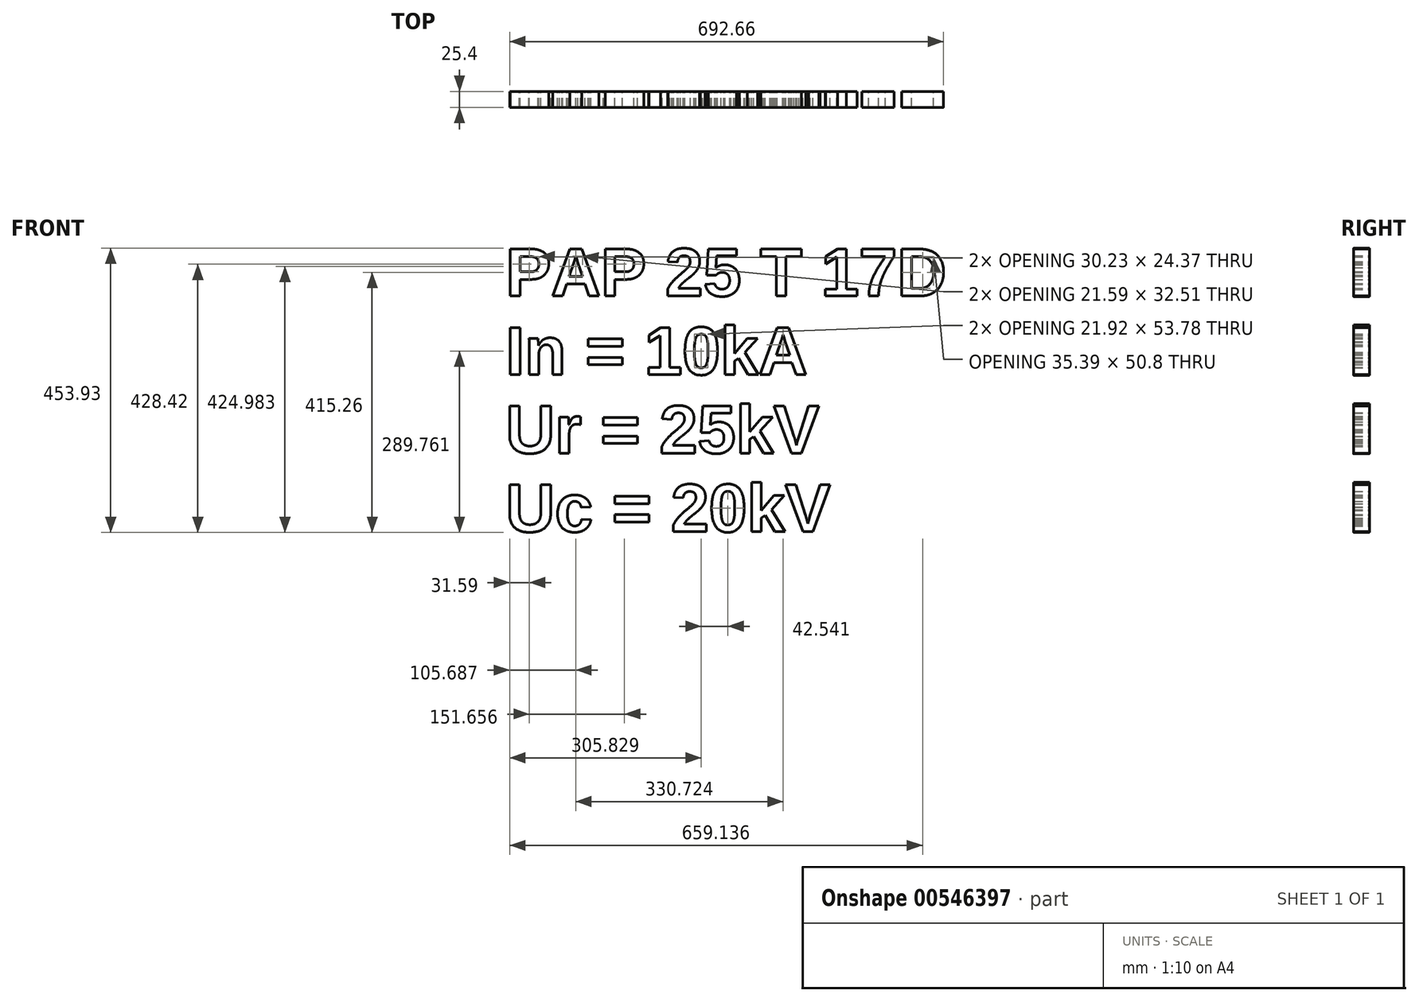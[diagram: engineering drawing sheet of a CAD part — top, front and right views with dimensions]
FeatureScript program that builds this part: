
annotation { "Feature Type Name" : "Feature", "Feature Type Description" : "" }
export const myFeature = defineFeature(function(context is Context, id is Id, definition is map)
    precondition{}
    {
        {
            var Q0;
            Q0=qCreatedBy(makeId("Front.planeOp"),FACE);
            var sketch = newSketch(context, id + "F0", { "sketchPlane" : qUnion([Q0])});
            skText(sketch, "E0", { "text": "PAP 25 T 17D\nIn = 10kA\nUr = 25kV\nUc = 20kV", "fontName": "Arimo-Bold.ttf"});
            const initialGuessF0  = {"E0": [-0.0624, -0.0381, 1, 0, 0.0786]};
            skSetInitialGuess(sketch, initialGuessF0);
            skSolve(sketch);
        }
        {
            var Q0;
            Q0 = qSketchRegion(id + "F0", true);
            extrude(context, id + "F1", {"entities" : qUnion([Q0]), "depth" : 25.4 * mm, "offsetDistance" : 25.4 * mm});
        }
    });
